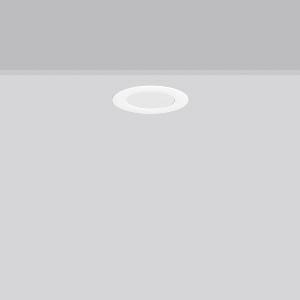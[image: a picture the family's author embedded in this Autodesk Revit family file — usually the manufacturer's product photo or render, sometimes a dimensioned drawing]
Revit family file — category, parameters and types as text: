
# Revit family: toledo_flat_round_e_901451_002_1_76_912b
name_source: partatom
category: Lighting Fixtures
units: mm (PartAtom-declared; Revit-internal decimal feet)

## family parameters
Cut with Voids When Loaded = No
Host = Face
Light Source = No
Part Type = Normal
Room Calculation Point = No
Round Connector Dimension = Use Diameter
Shared = No

## types (1)
- TOLEDO FLAT round E (1 x LED Modul 840, 530 lm, 4000)
    Apparent Load = 5 VA
    CIE Flux Codes = 48 79 96 100 100
    Color Rendering = 80
    Color Temperature = 4000
    Default Elevation = 1800 mm
    Description = Series: TOLEDO FLAT round
Ultra thin recessed downlight. Housing: die-cast aluminium. Light guide and diffuser made of non-yellowing PMMA, opal matt. Ceiling installation with spring system. Mounting depth depends on ceiling strength. Including separate LED converter with connecting cable 250 mm. Suitable for through-wiring with separately available accessories. Surface mounted housing as accessory for all sizes. Retrofittable decorative cylinders made of chintz fabric as accessory, optional with satin finish plastic diffuser. Through-wiring box (5 pole) available as accessory. 
Colour: white
Diameter: 148 mm
Height: 2 mm
Cut-out diameter: 128 mm
Recess height: 31-53 mm
Luminaire: recess height: 31-51 mm
Lamp: LED
Socket: without socket
Colour temperature: 4000K
Colour rendering index (CRI): 80
System power: 5 W
Rated luminous flux: 530 lm
Luminous efficiency: 106 lm/W
Control gear: Converter, dimmable, DALI
Protection class: II
Type of protection: IP 54
    Height = 0 mm  [stored 0 ft]
    Lamp = 1 x LED Modul 840
    Lamp Light Flux = 530 lm
    Lamp count = 1
    Length = 148 mm
    Lifetime = 50000 h
    Luminous efficacy = 106 lm/W
    Manufacturer = RZB
    ModVariant = No
    Model = 901451.002.1.76
    Mounting Place = Ceiling
    Mounting Type = Recessed
    Number of Poles = 1
    OnlyDefault = Yes
    Power Factor = 1
    Product Name = TOLEDO FLAT round E
    Product group = Recessed downlights
    ProductGroupID = 402
    Protection Class = Protection class II
    Protection Degree = IP 20
    RLX_Detail_Level = 1
    RLX_Emergency_Light_Flux = 0 lm
    RLX_Emergency_Type = 0
    RLX_Emergency_Type_DB = No
    RlxData = <blob elided: 74781 chars, md5=d0efe3f3>
    Socket = socket
    Standby Power = 0 W
    System Light Flux = 530 lm
    System Power = 5 W
    Type Comments = Product without accessories
    Type Image = 901451.002.jpg
    URL = http://relux.com
    VarID = ---
    Voltage = 230 V
    Voltage Range = 220-240 V
    Weight = 0.00 kg
    Width = 0 mm  [stored 0 ft]

note: [stored X ft] marks values corroborated as IEEE doubles in the binary element streams (Revit-internal decimal feet)

## geometry (parser evidence)
native form markers: Blend x4, Sweep x11
no freeform markers — native parametric forms only
